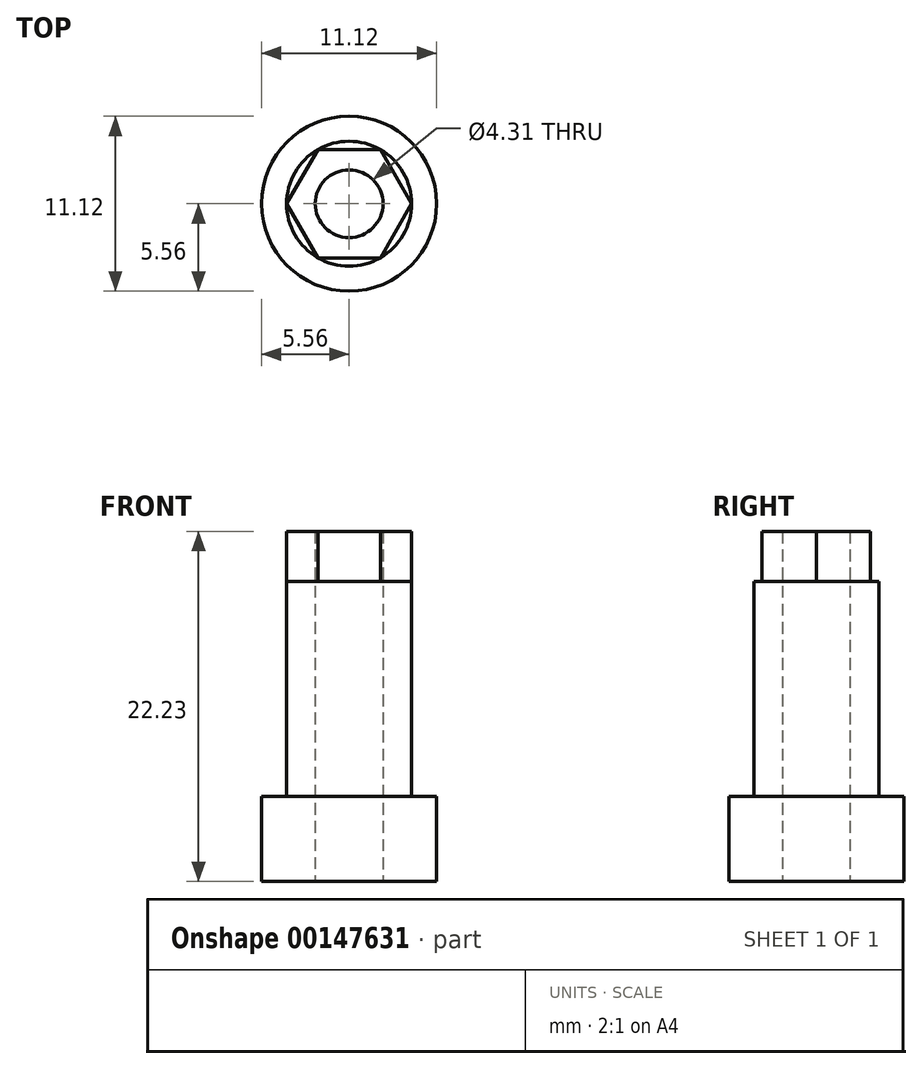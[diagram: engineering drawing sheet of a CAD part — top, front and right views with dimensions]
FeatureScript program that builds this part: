
annotation { "Feature Type Name" : "Feature", "Feature Type Description" : "" }
export const myFeature = defineFeature(function(context is Context, id is Id, definition is map)
    precondition{}
    {
        {
            var Q0;
            Q0=qCreatedBy(makeId("Top.planeOp"),FACE);
            var sketch = newSketch(context, id + "F0", { "sketchPlane" : qUnion([Q0])});
            skCircle(sketch, "E0", {"center": v(0, 0) * mm, "radius": 2.15 * mm});
            skCircle(sketch, "E1", {"center": v(0, 0) * mm, "radius": 5.56 * mm});
            skSolve(sketch);
        }
        {
            var Q0;
            Q0=qSketchRegion(id+"F0",true);
            extrude(context, id + "F1", {"entities" : qUnion([Q0]), "depth" : 5.4 * mm});
        }
        {
            var Q0;
            Q0=makeQuery(id+"F1.opExtrude","CAP_FACE",FACE,{"disambiguationData":[OSD([sQuery(id+"F0.wireOp",EDGE,"E0"),sQuery(id+"F0.wireOp",EDGE,"E1")])],"isStart":false});
            var sketch = newSketch(context, id + "F2", { "sketchPlane" : qUnion([Q0])});
            skCircle(sketch, "E2", {"center": v(0, 0) * mm, "radius": 2.15 * mm});
            skCircle(sketch, "E3", {"center": v(0, 0) * mm, "radius": 3.97 * mm});
            skSolve(sketch);
        }
        {
            var Q0;
            Q0=qSketchRegion(id+"F2",true);
            extrude(context, id + "F3", {"entities" : qUnion([Q0]), "operationType" : NewBodyOperationType.ADD, "depth" : 13.65 * mm});
        }
        {
            var Q0;
            Q0=makeQuery(id+"F3.opExtrude","CAP_FACE",FACE,{"disambiguationData":[OSD([sQuery(id+"F2.wireOp",EDGE,"E2"),sQuery(id+"F2.wireOp",EDGE,"E3")])],"isStart":false});
            var sketch = newSketch(context, id + "F4", { "sketchPlane" : qUnion([Q0])});
            skCircle(sketch, "E4.cCircle", {"center": v(0, 0) * mm, "radius": 3.97 * mm, "construction": true});
            skLineSegment(sketch, "E4.0", {"start": v(-1.98, 3.44) * mm, "end": v(1.98, 3.44) * mm});
            skLineSegment(sketch, "E4.1", {"start": v(1.98, 3.44) * mm, "end": v(3.97, 0) * mm});
            skLineSegment(sketch, "E4.2", {"start": v(3.97, 0) * mm, "end": v(1.98, -3.44) * mm});
            skLineSegment(sketch, "E4.3", {"start": v(1.98, -3.44) * mm, "end": v(-1.98, -3.44) * mm});
            skLineSegment(sketch, "E4.4", {"start": v(-1.98, -3.44) * mm, "end": v(-3.97, 0) * mm});
            skLineSegment(sketch, "E4.5", {"start": v(-3.97, 0) * mm, "end": v(-1.98, 3.44) * mm});
            skCircle(sketch, "E5", {"center": v(0, 0) * mm, "radius": 2.15 * mm});
            skSolve(sketch);
        }
        {
            var Q0;
            Q0=qSketchRegion(id+"F4",true);
            extrude(context, id + "F5", {"entities" : qUnion([Q0]), "operationType" : NewBodyOperationType.ADD, "depth" : 3.17 * mm});
        }
    });
